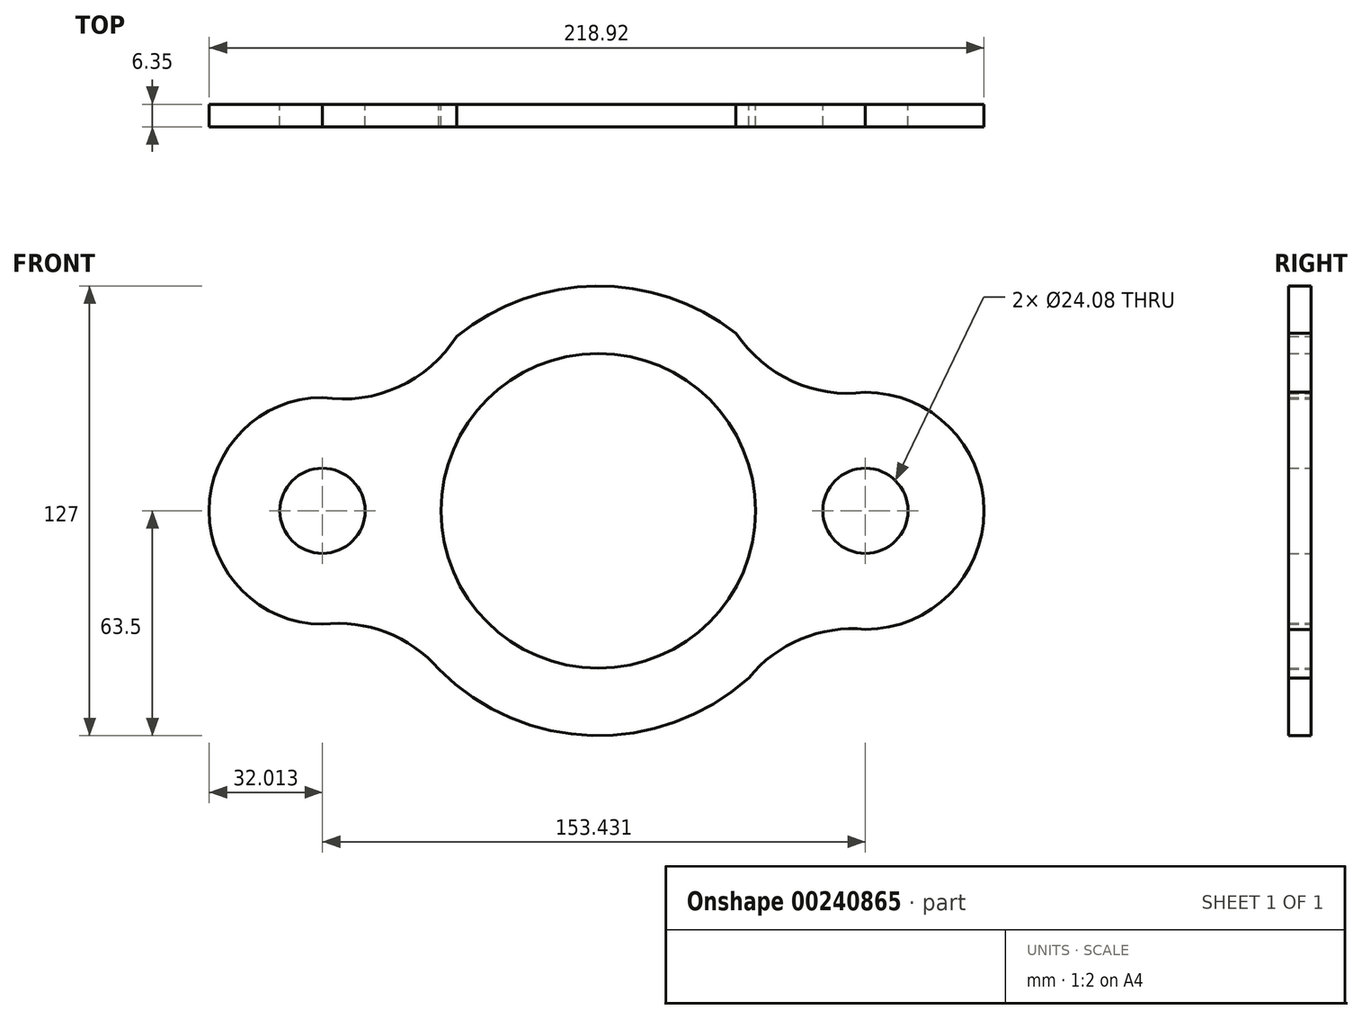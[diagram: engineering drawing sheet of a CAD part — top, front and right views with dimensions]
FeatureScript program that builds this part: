
annotation { "Feature Type Name" : "Feature", "Feature Type Description" : "" }
export const myFeature = defineFeature(function(context is Context, id is Id, definition is map)
    precondition{}
    {
        {
            var Q0;
            Q0=qCreatedBy(makeId("Front.planeOp"),FACE);
            var sketch = newSketch(context, id + "F0", { "sketchPlane" : qUnion([Q0])});
            skCircle(sketch, "E0", {"center": v(0, 0) * mm, "radius": 44.45 * mm});
            skSolve(sketch);
        }
        {
            var Q0;
            Q0=qCreatedBy(makeId("Front.planeOp"),FACE);
            var sketch = newSketch(context, id + "F1", { "sketchPlane" : qUnion([Q0])});
            skArc(sketch, "E1", {"start": v(38.9, 50.2) * mm, "mid": v(-0.72, 63.5) * mm, "end": v(-40.03, 49.3) * mm});
            skArc(sketch, "E2", {"start": v(42.48, -47.2) * mm, "mid": v(-1.77, -63.48) * mm, "end": v(-45.04, -44.76) * mm});
            skCircle(sketch, "E3", {"center": v(-77.96, 0) * mm, "radius": 12.04 * mm});
            skCircle(sketch, "E4", {"center": v(75.47, 0) * mm, "radius": 12.04 * mm});
            skArc(sketch, "E5", {"start": v(75.47, 33.47) * mm, "mid": v(108.95, 0) * mm, "end": v(75.47, -33.47) * mm});
            skArc(sketch, "E6", {"start": v(-77.96, 32) * mm, "mid": v(-109.97, 0) * mm, "end": v(-77.96, -32) * mm});
            skArc(sketch, "E7", {"start": v(-77.96, 32) * mm, "mid": v(-56.42, 35) * mm, "end": v(-40.03, 49.3) * mm});
            skArc(sketch, "E8", {"start": v(-45.04, -44.76) * mm, "mid": v(-59.93, -34.34) * mm, "end": v(-77.96, -32) * mm});
            skArc(sketch, "E9", {"start": v(38.9, 50.2) * mm, "mid": v(54.8, 36.61) * mm, "end": v(75.47, 33.47) * mm});
            skArc(sketch, "E10", {"start": v(75.47, -33.47) * mm, "mid": v(57.27, -36.23) * mm, "end": v(42.48, -47.2) * mm});
            skSolve(sketch);
        }
        {
            var Q0;
            Q0 = qSketchRegion(id + "F0", true);
            var Q1;
            Q1=makeQuery(id+"F1.imprint","IMPRINT",FACE,{"disambiguationData":[TD([[makeQuery(id+"F1.imprint","IMPRINT",EDGE,{"derivedFrom":sQuery(id+"F1.wireOp",EDGE,"E1")}),1.0]])]});
            extrude(context, id + "F2", {"entities" : qUnion([Q0, Q1]), "depth" : 6.35 * mm});
        }
    });
